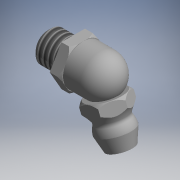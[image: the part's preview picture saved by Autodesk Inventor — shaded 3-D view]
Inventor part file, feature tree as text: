
AUTODESK INVENTOR PART (.ipt)
format: ipt  version: 2017.3 (Build 213256000, 256)  size: 216,576 bytes
history: native  units: mm (DEFAULTED — no unit token found)
features: other x7, sketch x5, revolve x3, extrude x2, thread x1
ambient origin geometry x8: Origin, YZ Plane, XZ Plane, XY Plane, X Axis, Y Axis, Z Axis, Center Point
bodies: Solid1 (feature_tree)
feature tree (18):
  revolve  "Revolution1"  [1 undecoded]
  thread  "Thread1"  [1 undecoded]
  revolve  "Revolution2"  Angle=360.0deg
  extrude  "Extrusion1"  TaperAngle=0.0deg  [1 undecoded]
  revolve  "Revolution3"  [1 undecoded]
  extrude  "Extrusion2"  [1 undecoded]
  other  "n_j_XY"
  other  "n_j_YZ"
  other  "n_j_ZX"
  other  "n_j_X"
  other  "n_j_Y"
  other  "n_j_Z"
  other  "n_j_Center"
  sketch  "Sketch_1"  dims[d0=360.0deg d1=3.84338mm d2=0.0mm d3=360.0deg]
  sketch  "Sketch_5"  dims[d4=5.0mm d5=0.0mm d6=360.0deg]
  sketch  "Sketch_13"  dims[d7=2.5mm d8=0.0mm d9=0.0mm]
  sketch  "Sketch_17"
  sketch  "Sketch_18"
note: 5 required parameter values undecoded (feature->parameter linkage not recoverable at this tier; creation-order binding heuristic only, values carry confidence <= 0.55)